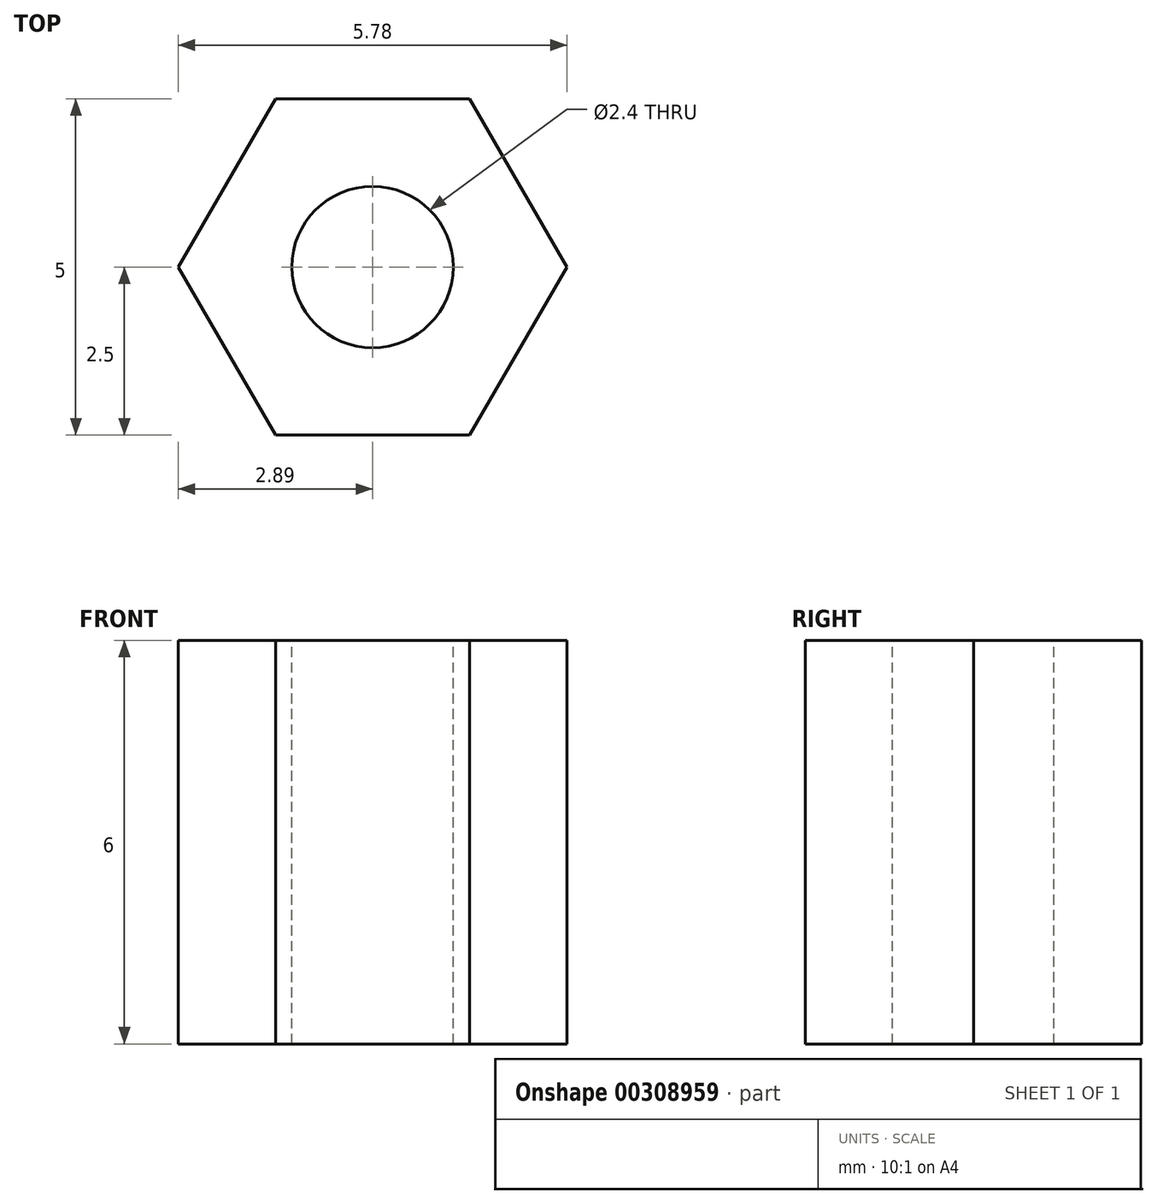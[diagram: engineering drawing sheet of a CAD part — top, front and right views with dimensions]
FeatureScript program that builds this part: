
annotation { "Feature Type Name" : "Feature", "Feature Type Description" : "" }
export const myFeature = defineFeature(function(context is Context, id is Id, definition is map)
    precondition{}
    {
        {
            var Q0;
            Q0=qCreatedBy(makeId("Top.planeOp"),FACE);
            var sketch = newSketch(context, id + "F0", { "sketchPlane" : qUnion([Q0])});
            skCircle(sketch, "E0.cCircle", {"center": v(0, 0) * mm, "radius": 2.5 * mm, "construction": true});
            skLineSegment(sketch, "E0.0", {"start": v(-1.44, 2.5) * mm, "end": v(1.44, 2.5) * mm});
            skLineSegment(sketch, "E0.1", {"start": v(1.44, 2.5) * mm, "end": v(2.89, 0) * mm});
            skLineSegment(sketch, "E0.2", {"start": v(2.89, 0) * mm, "end": v(1.44, -2.5) * mm});
            skLineSegment(sketch, "E0.3", {"start": v(1.44, -2.5) * mm, "end": v(-1.44, -2.5) * mm});
            skLineSegment(sketch, "E0.4", {"start": v(-1.44, -2.5) * mm, "end": v(-2.89, 0) * mm});
            skLineSegment(sketch, "E0.5", {"start": v(-2.89, 0) * mm, "end": v(-1.44, 2.5) * mm});
            skPoint(sketch, "E0.0.midPoint", {"position": v(0, 2.5) * mm});
            skSolve(sketch);
        }
        {
            var Q0;
            Q0=makeQuery(id+"F0.imprint","IMPRINT",FACE,{"disambiguationData":[TD([[makeQuery(id+"F0.imprint","IMPRINT",EDGE,{"derivedFrom":sQuery(id+"F0.wireOp",EDGE,"E0.0")}),-1.0]])]});
            extrude(context, id + "F1", {"entities" : qUnion([Q0]), "offsetDistance" : 25 * mm, "depth" : 6 * mm});
        }
        {
            var Q0;
            Q0=makeQuery(id+"F1.opExtrude","CAP_FACE",FACE,{"disambiguationData":[OSD([sQuery(id+"F0.wireOp",EDGE,"E0.0"),sQuery(id+"F0.wireOp",EDGE,"E0.1"),sQuery(id+"F0.wireOp",EDGE,"E0.2"),sQuery(id+"F0.wireOp",EDGE,"E0.3"),sQuery(id+"F0.wireOp",EDGE,"E0.4"),sQuery(id+"F0.wireOp",EDGE,"E0.5")])],"isStart":false});
            var sketch = newSketch(context, id + "F2", { "sketchPlane" : qUnion([Q0])});
            skPoint(sketch, "E1", {"position": v(0, 0) * mm});
            skSolve(sketch);
        }
        {
            var Q0;
            Q0=sQuery(id+"F2.wireOp",VERTEX,"E1");
            var Q1;
            Q1=makeQuery(id+"F1.opExtrude","SWEPT_BODY",BODY,{"disambiguationData":[OSD([sQuery(id+"F0.wireOp",EDGE,"E0.0"),sQuery(id+"F0.wireOp",EDGE,"E0.1"),sQuery(id+"F0.wireOp",EDGE,"E0.2"),sQuery(id+"F0.wireOp",EDGE,"E0.3"),sQuery(id+"F0.wireOp",EDGE,"E0.4"),sQuery(id+"F0.wireOp",EDGE,"E0.5")])]});
            hole(context, id + "F3", {"style" : HoleStyle.SIMPLE, "endStyle" : HoleEndStyle.THROUGH, "standardTappedOrClearance" : lookupTablePath({ "standard" : "ISO", "engagement" : "75%", "pitch" : "0.6 mm", "size" : "M3", "type" : "Tapped" }), "standardBlindInLast" : lookupTablePath({ "standard" : "ISO", "engagement" : "75%", "pitch" : "0.6 mm", "size" : "M3", "type" : "Tapped" }), "holeDiameter" : 2.4 * mm, "showTappedDepth" : true, "tappedDepth" : 12 * mm, "tapClearance" : 3, "locations" : qUnion([Q0]), "scope" : qUnion([Q1])});
        }
    });
